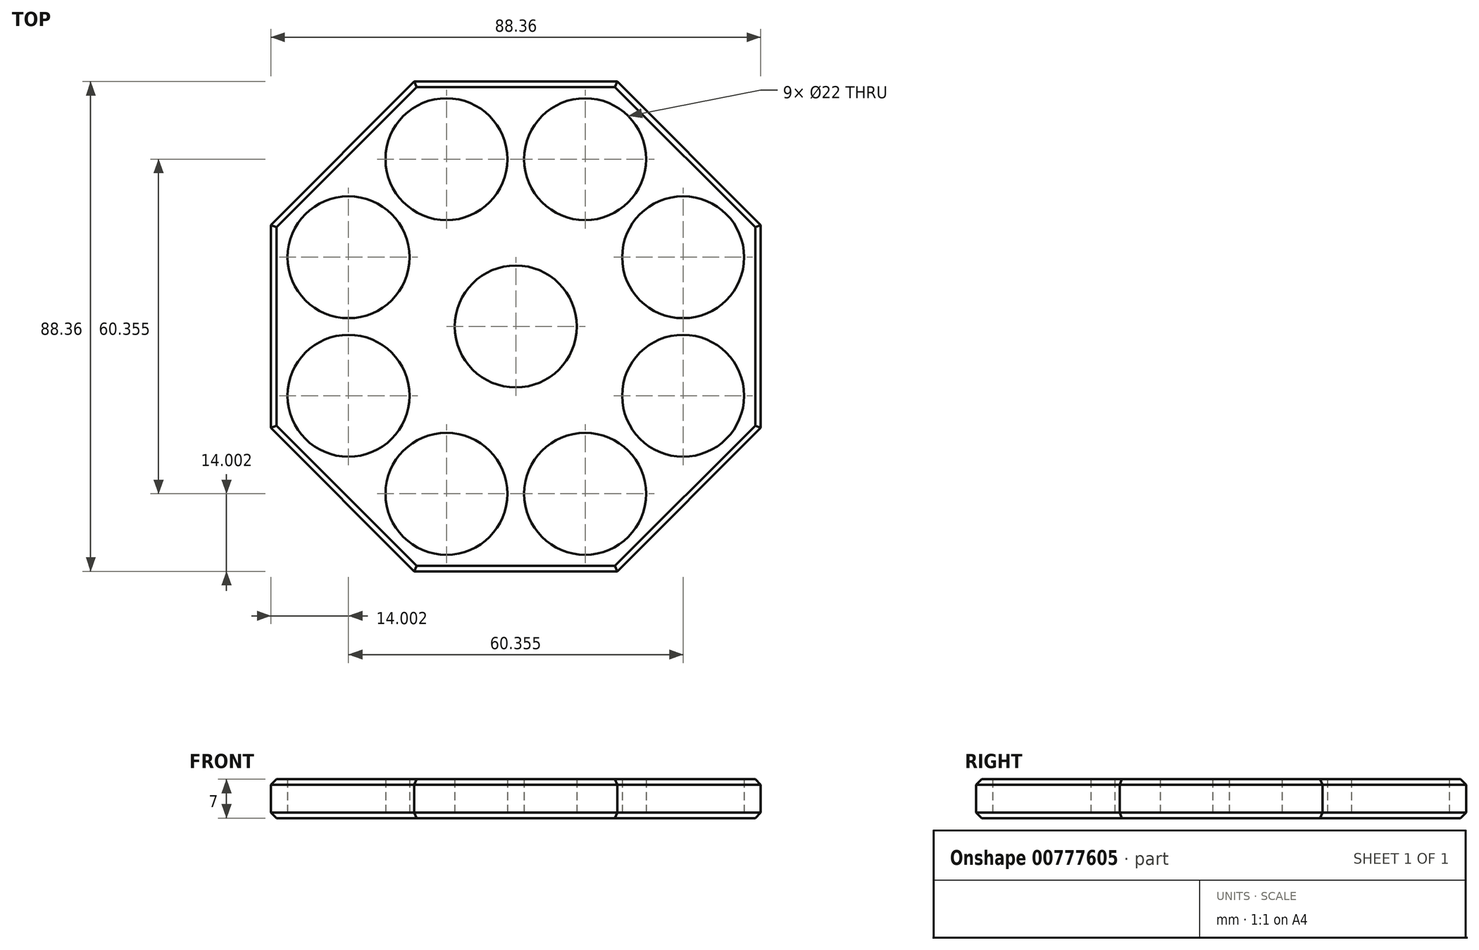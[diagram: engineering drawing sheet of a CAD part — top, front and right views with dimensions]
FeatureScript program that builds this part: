
annotation { "Feature Type Name" : "Feature", "Feature Type Description" : "" }
export const myFeature = defineFeature(function(context is Context, id is Id, definition is map)
    precondition{}
    {
        {
            var Q0;
            Q0=qCreatedBy(makeId("Top.planeOp"),FACE);
            var sketch = newSketch(context, id + "F0", { "sketchPlane" : qUnion([Q0])});
            skCircle(sketch, "E0", {"center": v(0, 0) * mm, "radius": 11 * mm});
            skPoint(sketch, "E1.0.midPoint", {"position": v(30.18, 0) * mm});
            skCircle(sketch, "E2", {"center": v(-12.5, 30.18) * mm, "radius": 11 * mm});
            skCircle(sketch, "E3.1.0", {"center": v(-30.18, 12.5) * mm, "radius": 11 * mm});
            skCircle(sketch, "E3.2.0", {"center": v(-30.18, -12.5) * mm, "radius": 11 * mm});
            skArc(sketch, "E3.2.1", {"start": v(-30.14, 1.5) * mm, "mid": v(-30.16, 1.5) * mm, "end": v(-30.18, 1.5) * mm});
            skCircle(sketch, "E3.3.0", {"center": v(-12.5, -30.18) * mm, "radius": 11 * mm});
            skArc(sketch, "E3.3.1", {"start": v(-22.37, -20.25) * mm, "mid": v(-22.39, -20.26) * mm, "end": v(-22.4, -20.28) * mm});
            skCircle(sketch, "E3.4.0", {"center": v(12.5, -30.18) * mm, "radius": 11 * mm});
            skArc(sketch, "E3.4.1", {"start": v(-1.5, -30.14) * mm, "mid": v(-1.5, -30.16) * mm, "end": v(-1.5, -30.18) * mm});
            skCircle(sketch, "E3.5.0", {"center": v(30.18, -12.5) * mm, "radius": 11 * mm});
            skCircle(sketch, "E3.6.0", {"center": v(30.18, 12.5) * mm, "radius": 11 * mm});
            skArc(sketch, "E3.6.1", {"start": v(30.14, -1.5) * mm, "mid": v(30.16, -1.5) * mm, "end": v(30.18, -1.5) * mm});
            skCircle(sketch, "E3.7.0", {"center": v(12.5, 30.18) * mm, "radius": 11 * mm});
            skArc(sketch, "E3.7.1", {"start": v(-1.5, 30.18) * mm, "mid": v(-1.5, 30.16) * mm, "end": v(-1.5, 30.14) * mm});
            skArc(sketch, "E4.trimOffspring", {"start": v(1.5, 30.14) * mm, "mid": v(1.5, 30.16) * mm, "end": v(1.5, 30.18) * mm});
            skArc(sketch, "E5.trimOffspring", {"start": v(-22.4, 20.28) * mm, "mid": v(-22.39, 20.26) * mm, "end": v(-22.37, 20.25) * mm});
            skArc(sketch, "E6.trimOffspring", {"start": v(-20.25, 22.37) * mm, "mid": v(-20.26, 22.39) * mm, "end": v(-20.28, 22.4) * mm});
            skArc(sketch, "E7.trimOffspring", {"start": v(-30.18, -1.5) * mm, "mid": v(-30.16, -1.5) * mm, "end": v(-30.14, -1.5) * mm});
            skArc(sketch, "E8.trimOffspring", {"start": v(-20.28, -22.4) * mm, "mid": v(-20.26, -22.39) * mm, "end": v(-20.25, -22.37) * mm});
            skArc(sketch, "E9.trimOffspring", {"start": v(1.5, -30.18) * mm, "mid": v(1.5, -30.16) * mm, "end": v(1.5, -30.14) * mm});
            skArc(sketch, "E10.trimOffspring", {"start": v(22.4, -20.28) * mm, "mid": v(22.39, -20.26) * mm, "end": v(22.37, -20.25) * mm});
            skArc(sketch, "E11.trimOffspring", {"start": v(20.25, -22.37) * mm, "mid": v(20.26, -22.39) * mm, "end": v(20.28, -22.4) * mm});
            skArc(sketch, "E12.trimOffspring", {"start": v(30.18, 1.5) * mm, "mid": v(30.16, 1.5) * mm, "end": v(30.14, 1.5) * mm});
            skArc(sketch, "E13.trimOffspring", {"start": v(20.28, 22.4) * mm, "mid": v(20.26, 22.39) * mm, "end": v(20.25, 22.37) * mm});
            skArc(sketch, "E14.trimOffspring", {"start": v(22.37, 20.25) * mm, "mid": v(22.39, 20.26) * mm, "end": v(22.4, 20.28) * mm});
            skLineSegment(sketch, "E15.0", {"start": v(44.18, 18.3) * mm, "end": v(44.18, -18.3) * mm});
            skLineSegment(sketch, "E15.1", {"start": v(44.18, -18.3) * mm, "end": v(18.3, -44.18) * mm});
            skLineSegment(sketch, "E15.2", {"start": v(18.3, -44.18) * mm, "end": v(-18.3, -44.18) * mm});
            skLineSegment(sketch, "E15.3", {"start": v(-18.3, -44.18) * mm, "end": v(-44.18, -18.3) * mm});
            skLineSegment(sketch, "E15.4", {"start": v(-44.18, -18.3) * mm, "end": v(-44.18, 18.3) * mm});
            skLineSegment(sketch, "E15.5", {"start": v(-44.18, 18.3) * mm, "end": v(-18.3, 44.18) * mm});
            skLineSegment(sketch, "E15.6", {"start": v(-18.3, 44.18) * mm, "end": v(18.3, 44.18) * mm});
            skLineSegment(sketch, "E15.7", {"start": v(18.3, 44.18) * mm, "end": v(44.18, 18.3) * mm});
            skSolve(sketch);
        }
        {
            var Q0;
            Q0=makeQuery(id+"F0.imprint","IMPRINT",FACE,{"disambiguationData":[TD([[makeQuery(id+"F0.imprint","IMPRINT",EDGE,{"derivedFrom":sQuery(id+"F0.wireOp",EDGE,"E0")}),-1.0]])]});
            extrude(context, id + "F1", {"entities" : qUnion([Q0]), "depth" : 7 * mm, "offsetDistance" : 25 * mm});
        }
        {
            var Q0;
            Q0=makeQuery(id+"F1.opExtrude","CAP_EDGE",EDGE,{"disambiguationData":[OSD([sQuery(id+"F0.wireOp",EDGE,"E15.5")])],"isStart":true});
            var Q1;
            Q1=makeQuery(id+"F1.opExtrude","CAP_EDGE",EDGE,{"disambiguationData":[OSD([sQuery(id+"F0.wireOp",EDGE,"E15.4")])],"isStart":true});
            var Q2;
            Q2=makeQuery(id+"F1.opExtrude","CAP_EDGE",EDGE,{"disambiguationData":[OSD([sQuery(id+"F0.wireOp",EDGE,"E15.3")])],"isStart":true});
            var Q3;
            Q3=makeQuery(id+"F1.opExtrude","CAP_EDGE",EDGE,{"disambiguationData":[OSD([sQuery(id+"F0.wireOp",EDGE,"E15.2")])],"isStart":true});
            var Q4;
            Q4=makeQuery(id+"F1.opExtrude","CAP_EDGE",EDGE,{"disambiguationData":[OSD([sQuery(id+"F0.wireOp",EDGE,"E15.1")])],"isStart":true});
            var Q5;
            Q5=makeQuery(id+"F1.opExtrude","CAP_EDGE",EDGE,{"disambiguationData":[OSD([sQuery(id+"F0.wireOp",EDGE,"E15.0")])],"isStart":true});
            var Q6;
            Q6=makeQuery(id+"F1.opExtrude","CAP_EDGE",EDGE,{"disambiguationData":[OSD([sQuery(id+"F0.wireOp",EDGE,"E15.6")])],"isStart":true});
            var Q7;
            Q7=makeQuery(id+"F1.opExtrude","CAP_EDGE",EDGE,{"disambiguationData":[OSD([sQuery(id+"F0.wireOp",EDGE,"E15.7")])],"isStart":true});
            var Q8;
            Q8=makeQuery(id+"F1.opExtrude","CAP_EDGE",EDGE,{"disambiguationData":[OSD([sQuery(id+"F0.wireOp",EDGE,"E15.7")])],"isStart":false});
            var Q9;
            Q9=makeQuery(id+"F1.opExtrude","CAP_EDGE",EDGE,{"disambiguationData":[OSD([sQuery(id+"F0.wireOp",EDGE,"E15.0")])],"isStart":false});
            var Q10;
            Q10=makeQuery(id+"F1.opExtrude","CAP_EDGE",EDGE,{"disambiguationData":[OSD([sQuery(id+"F0.wireOp",EDGE,"E15.1")])],"isStart":false});
            var Q11;
            Q11=makeQuery(id+"F1.opExtrude","CAP_EDGE",EDGE,{"disambiguationData":[OSD([sQuery(id+"F0.wireOp",EDGE,"E15.2")])],"isStart":false});
            var Q12;
            Q12=makeQuery(id+"F1.opExtrude","CAP_EDGE",EDGE,{"disambiguationData":[OSD([sQuery(id+"F0.wireOp",EDGE,"E15.3")])],"isStart":false});
            var Q13;
            Q13=makeQuery(id+"F1.opExtrude","CAP_EDGE",EDGE,{"disambiguationData":[OSD([sQuery(id+"F0.wireOp",EDGE,"E15.5")])],"isStart":false});
            var Q14;
            Q14=makeQuery(id+"F1.opExtrude","CAP_EDGE",EDGE,{"disambiguationData":[OSD([sQuery(id+"F0.wireOp",EDGE,"E15.4")])],"isStart":false});
            var Q15;
            Q15=makeQuery(id+"F1.opExtrude","CAP_EDGE",EDGE,{"disambiguationData":[OSD([sQuery(id+"F0.wireOp",EDGE,"E15.6")])],"isStart":false});
            chamfer(context, id + "F2", {"entities" : qUnion([Q0, Q1, Q2, Q3, Q4, Q5, Q6, Q7, Q8, Q9, Q10, Q11, Q12, Q13, Q14, Q15]), "width" : 1 * mm, "tangentPropagation" : true});
        }
    });
